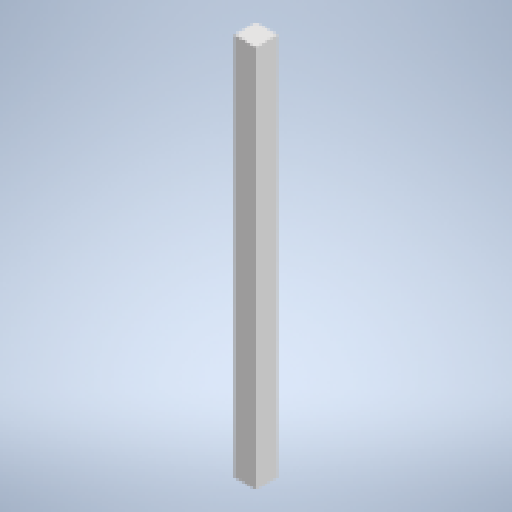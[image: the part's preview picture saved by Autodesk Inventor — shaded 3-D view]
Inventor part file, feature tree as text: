
AUTODESK INVENTOR PART (.ipt)
format: ipt  version: 2024 (Build 280153000, 153)  size: 134,656 bytes
history: native  units: mm
features: extrude x1, sketch x1
ambient origin geometry x8: Origin, YZ Plane, XZ Plane, XY Plane, X Axis, Y Axis, Z Axis, Center Point
bodies: Solid1 (feature_tree)
feature tree (2):
  extrude  "Extrusion1"  Depth=45.0mm
  sketch  "Sketch1"  dims[d0=45.0mm d1=45.0mm d2=800.0mm d3=0.0mm]
